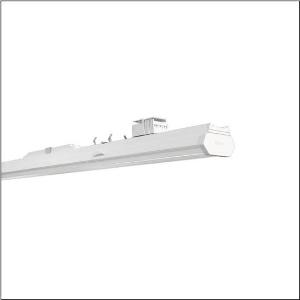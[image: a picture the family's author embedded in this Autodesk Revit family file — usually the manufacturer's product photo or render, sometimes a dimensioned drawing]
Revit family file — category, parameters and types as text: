
# Revit family: licross_21_protected_ho_52tp11dn4dxs
name_source: partatom
category: Lighting Fixtures
units: mm (PartAtom-declared; Revit-internal decimal feet)

## family parameters
Cut with Voids When Loaded = No
Host = Face
Light Source = No
Part Type = Normal
Room Calculation Point = No
Round Connector Dimension = Use Diameter
Shared = No

## types (1)
- --- (1 x LED, 13000 lm, 73.1 W, 4000K)
    Apparent Load = 73 VA
    CIE Flux Codes = 84 94 98 99 100
    Color Rendering = 80
    Color Temperature = 4000K
    Default Elevation = 1800 mm
    Description = Licross 21 Protected HO, luminaire insert, of sheet steel, galvanised, coil coated, white, length: 1.500mm, width: 90mm, height: 103mm, LED rated luminous flux: 13.000lm, light colour: 840, SDCM (Standard Deviation of Colour Matching)MacAdam ≤ 3 SDCM (initial), control gear: DALI 2, with plug, 5-pole, with phase selection, mains connection: 220..240V, AC, 50/60Hz, rated input power: 73W, internal wiring halogen-free, primary light control with lens, of plastic, primary optical cover: cover, of PMMA, light emission: direct distribution, primary light characteristic: symmetric, protection rating (complete): IP64, insulation class (complete): insulation class I (protective earthing), certification: CE, ENEC, VDE, UKCA, protection symbol: D if used in an environment with conductive dust loads with corresponding accessories, impact resistance: IK06, permissible ambient temperature for indoor applications: -25..+40°C, corresponds to IFS (International Featured Standards) requirements for safety and quality in the food industry, reducing of maximum allowable ambient temperature of 5°C with ceiling mounting, LABS conformity tested according to VDMA 24364:2018-05, The light source and the operating device comply with the requirements of the Ecodesign Regulation (EU) 2019/2020 and are replaceable in accordance with this regulation, packaging unit: 1 piece
    Height = 92 mm
    Lamp = 1 x LED
    Lamp Light Flux = 13000 lm
    Lamp Power = 73.1 W
    Lamp count = 1
    Length = 1500 mm
    Luminous efficacy = 178 lm/W
    Manufacturer = Siteco
    ModVariant = No
    Model = 52TP11DN4DXS
    Mounting Place = Ceiling
    Mounting Type = Pendant
    Number of Poles = 1
    OnlyDefault = Yes
    Power Factor = 1
    Product Name = Licross 21 Protected HO
    Product group = luminaire insert | ceiling pendant
    ProductGroupID = 901
    Protection Class = Protection class I
    Protection Degree = IP 64
    RLX_Detail_Level = 1
    RLX_Emergency_Light_Flux = 0 lm
    RLX_Emergency_Type = 0
    RLX_Emergency_Type_DB = No
    RlxData = <blob elided: 24621 chars, md5=72c3de35>
    Socket = socket
    Standby Power = 0 W
    System Light Flux = 13000 lm
    System Power = 73 W
    Type Comments = factory setting: luminous flux: 100 % | dim-lin: 254 | 417 mA
    Type Image = l_1256148.jpg
    URL = http://relux.com
    VarID = @adj_130065
    Voltage = 0 V
    Weight = 0.00 kg
    Width = 88 mm

## geometry (parser evidence)
native form markers: Blend x4, Sweep x11
no freeform markers — native parametric forms only
